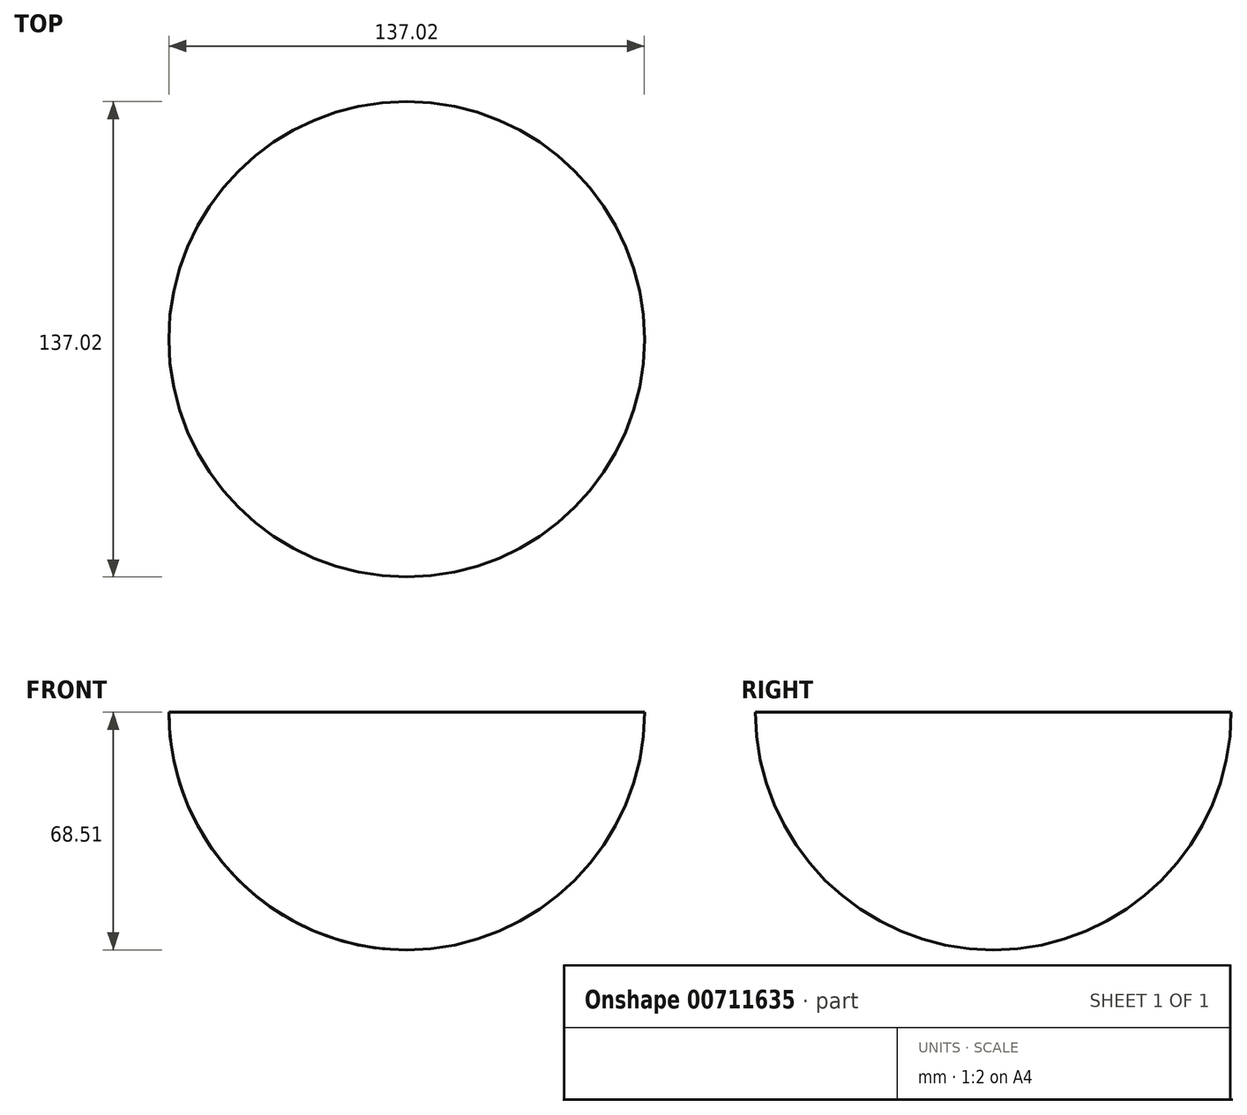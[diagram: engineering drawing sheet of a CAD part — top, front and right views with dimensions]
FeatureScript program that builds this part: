
annotation { "Feature Type Name" : "Feature", "Feature Type Description" : "" }
export const myFeature = defineFeature(function(context is Context, id is Id, definition is map)
    precondition{}
    {
        {
            var Q0;
            Q0=qCreatedBy(makeId("Front.planeOp"),FACE);
            var sketch = newSketch(context, id + "F0", { "sketchPlane" : qUnion([Q0])});
            skArc(sketch, "E0", {"start": v(68.51, 0) * mm, "mid": v(48.44, -48.44) * mm, "end": v(0, -68.51) * mm});
            skLineSegment(sketch, "E1", {"start": v(0, 0) * mm, "end": v(0, -68.51) * mm});
            skLineSegment(sketch, "E2", {"start": v(68.51, 0) * mm, "end": v(0, 0) * mm});
            skSolve(sketch);
        }
        {
            var Q0;
            Q0=qSketchRegion(id+"F0",true);
            var Q1;
            Q1=sQuery(id+"F0.wireOp",EDGE,"E1");
            revolve(context, id + "F1", {"surfaceOperationType" : NewSurfaceOperationType.ADD, "entities" : qUnion([Q0]), "axis" : qUnion([Q1]), "revolveType" : RevolveType.FULL});
        }
    });
